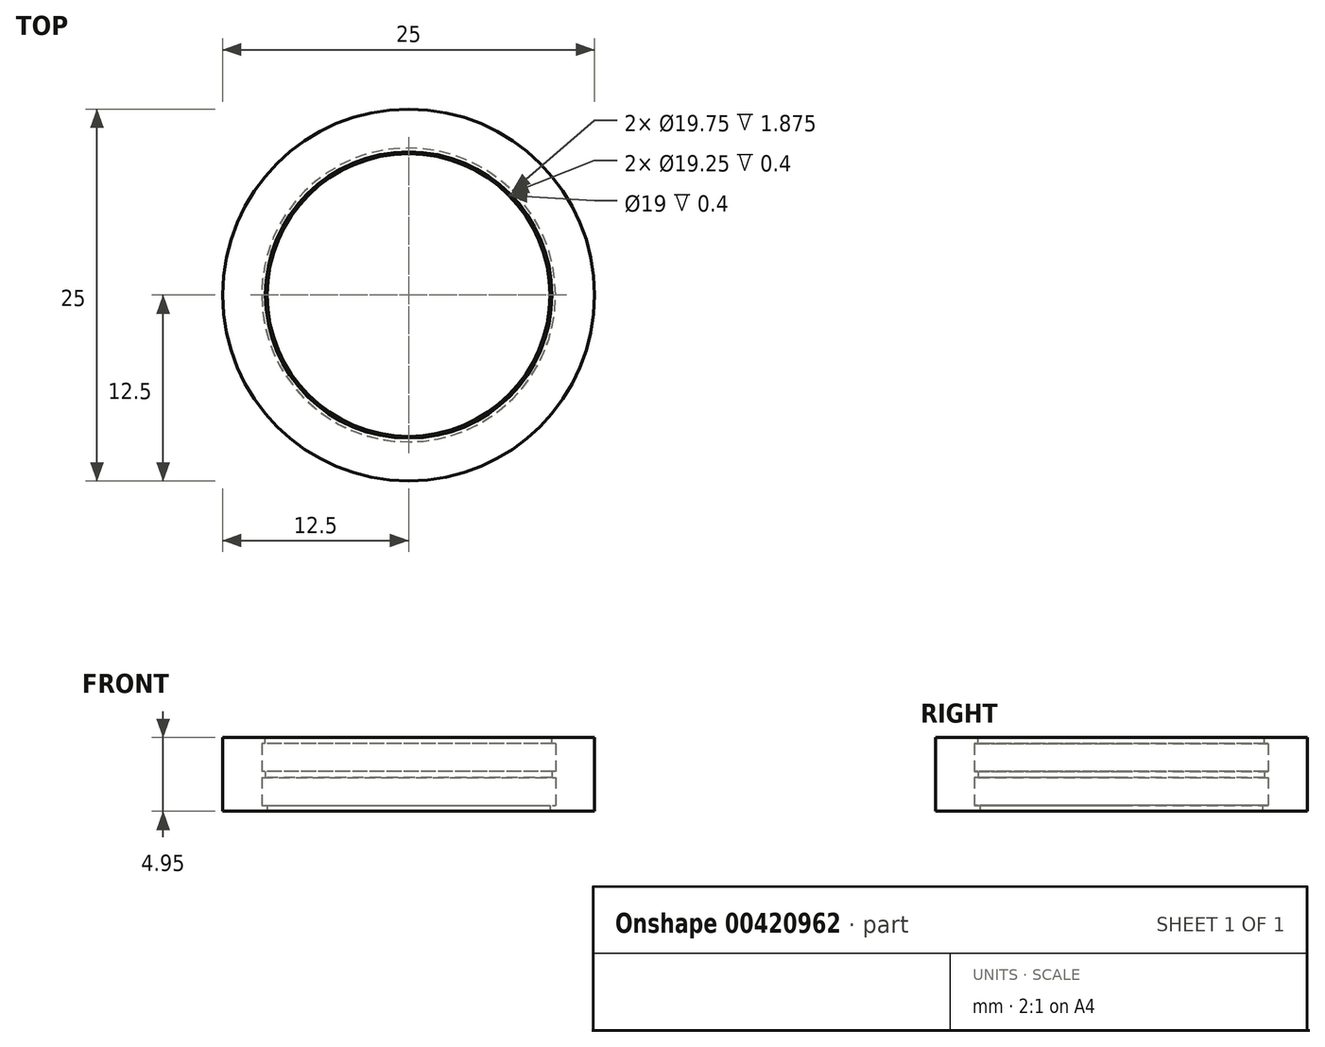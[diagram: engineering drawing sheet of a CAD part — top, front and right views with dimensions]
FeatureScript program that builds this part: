
annotation { "Feature Type Name" : "Feature", "Feature Type Description" : "" }
export const myFeature = defineFeature(function(context is Context, id is Id, definition is map)
    precondition{}
    {
        {
            var Q0;
            Q0=qCreatedBy(makeId("Top.planeOp"),FACE);
            var sketch = newSketch(context, id + "F0", { "sketchPlane" : qUnion([Q0])});
            skCircle(sketch, "E0", {"center": v(0, 0) * mm, "radius": 9.88 * mm});
            skCircle(sketch, "E1", {"center": v(0, 0) * mm, "radius": 12.5 * mm});
            skSolve(sketch);
        }
        {
            var Q0;
            Q0=makeQuery(id+"F0.imprint","IMPRINT",FACE,{"disambiguationData":[TD([[makeQuery(id+"F0.imprint","IMPRINT",EDGE,{"derivedFrom":sQuery(id+"F0.wireOp",EDGE,"E0")}),-1.0]])]});
            extrude(context, id + "F1", {"entities" : qUnion([Q0]), "depth" : 4.95 * mm});
        }
        {
            var Q0;
            Q0=qCreatedBy(makeId("Top.planeOp"),FACE);
            cPlane(context, id + "F2", {"entities" : qUnion([Q0]), "cplaneType" : CPlaneType.OFFSET, "offset" : 2.48 * mm, "width" : 150 * mm, "height" : 150 * mm});
        }
        {
            var Q0;
            Q0=qCreatedBy(id+"F2.planeOp",FACE);
            var sketch = newSketch(context, id + "F3", { "sketchPlane" : qUnion([Q0])});
            skCircle(sketch, "E2", {"center": v(0, 0) * mm, "radius": 9.62 * mm});
            skCircle(sketch, "E3", {"center": v(0, 0) * mm, "radius": 9.88 * mm});
            skSolve(sketch);
        }
        {
            var Q0;
            Q0=makeQuery(id+"F3.imprint","IMPRINT",FACE,{"disambiguationData":[TD([[makeQuery(id+"F3.imprint","IMPRINT",EDGE,{"derivedFrom":sQuery(id+"F3.wireOp",EDGE,"E2")}),-1.0]])]});
            extrude(context, id + "F4", {"entities" : qUnion([Q0]), "operationType" : NewBodyOperationType.ADD, "endBound" : BoundingType.SYMMETRIC, "depth" : 0.4 * mm});
        }
        {
            var Q0;
            Q0=makeQuery(id+"F1.opExtrude","CAP_FACE",FACE,{"disambiguationData":[OSD([sQuery(id+"F0.wireOp",EDGE,"E0"),sQuery(id+"F0.wireOp",EDGE,"E1")])],"isStart":true});
            cPlane(context, id + "F5", {"entities" : qUnion([Q0]), "cplaneType" : CPlaneType.OFFSET, "offset" : 0 * mm, "width" : 150 * mm, "height" : 150 * mm});
        }
        {
            var Q0;
            Q0=qCreatedBy(id+"F5.planeOp",FACE);
            var sketch = newSketch(context, id + "F6", { "sketchPlane" : qUnion([Q0])});
            skCircle(sketch, "E4", {"center": v(0, 0) * mm, "radius": 9.5 * mm});
            skCircle(sketch, "E5", {"center": v(0, 0) * mm, "radius": 9.88 * mm});
            skSolve(sketch);
        }
        {
            var Q0;
            Q0=makeQuery(id+"F6.imprint","IMPRINT",FACE,{"disambiguationData":[TD([[makeQuery(id+"F6.imprint","IMPRINT",EDGE,{"derivedFrom":sQuery(id+"F6.wireOp",EDGE,"E4")}),-1.0]])]});
            extrude(context, id + "F7", {"entities" : qUnion([Q0]), "operationType" : NewBodyOperationType.ADD, "depth" : -.4 * mm});
        }
        {
            var Q0;
            Q0=makeQuery(id+"F1.opExtrude","CAP_FACE",FACE,{"disambiguationData":[OSD([sQuery(id+"F0.wireOp",EDGE,"E0"),sQuery(id+"F0.wireOp",EDGE,"E1")])],"isStart":false});
            cPlane(context, id + "F8", {"entities" : qUnion([Q0]), "cplaneType" : CPlaneType.OFFSET, "offset" : 0 * mm, "width" : 150 * mm, "height" : 150 * mm});
        }
        {
            var Q0;
            Q0=qCreatedBy(id+"F8.planeOp",FACE);
            var sketch = newSketch(context, id + "F9", { "sketchPlane" : qUnion([Q0])});
            skCircle(sketch, "E6", {"center": v(0, 0) * mm, "radius": 9.62 * mm});
            skCircle(sketch, "E7", {"center": v(0, 0) * mm, "radius": 9.88 * mm});
            skLineSegment(sketch, "E8.bottom", {"start": v(0.12, -12.81) * mm, "end": v(-0.13, -12.81) * mm});
            skLineSegment(sketch, "E8.top", {"start": v(0.12, -8.58) * mm, "end": v(-0.13, -8.58) * mm});
            skLineSegment(sketch, "E8.left", {"start": v(0.12, -12.81) * mm, "end": v(0.12, -8.58) * mm});
            skLineSegment(sketch, "E8.right", {"start": v(-0.13, -12.81) * mm, "end": v(-0.13, -8.58) * mm});
            skPoint(sketch, "E8.middle", {"position": v(0, -10.7) * mm});
            skSolve(sketch);
        }
        {
            var Q0;
            Q0=makeQuery(id+"F9.imprint","IMPRINT",FACE,{"disambiguationData":[TD([[makeQuery(id+"F9.imprint","IMPRINT",EDGE,{"derivedFrom":sQuery(id+"F9.wireOp",EDGE,"E6")}),-1.0]])]});
            extrude(context, id + "F10", {"entities" : qUnion([Q0]), "operationType" : NewBodyOperationType.ADD, "depth" : -.4 * mm});
        }
    });
